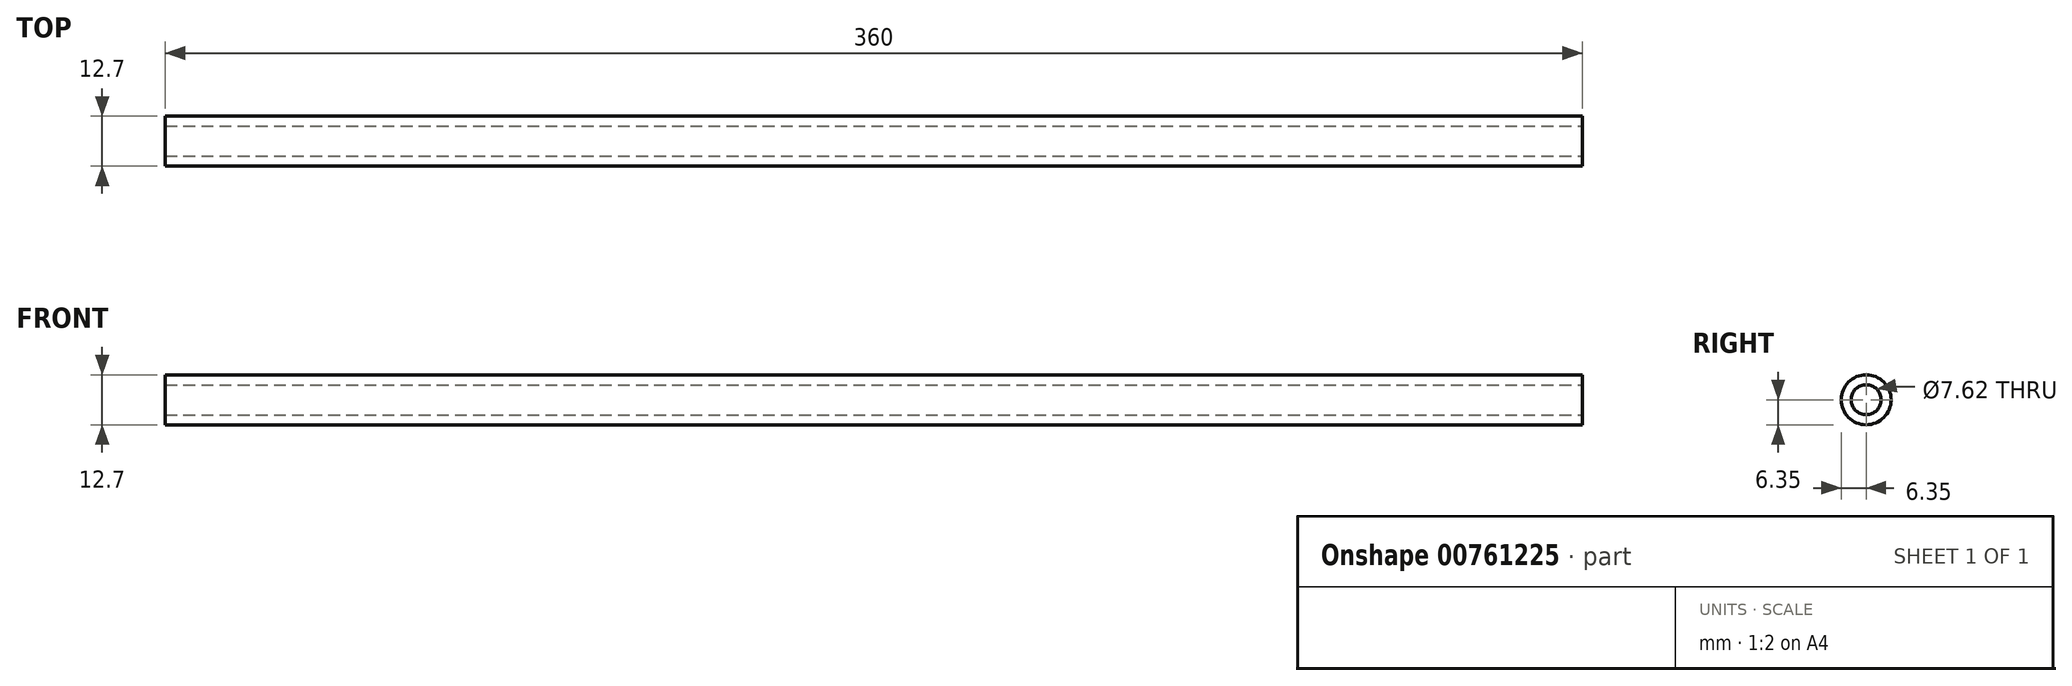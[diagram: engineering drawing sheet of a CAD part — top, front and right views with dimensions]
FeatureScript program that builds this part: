
annotation { "Feature Type Name" : "Feature", "Feature Type Description" : "" }
export const myFeature = defineFeature(function(context is Context, id is Id, definition is map)
    precondition{}
    {
        {
            var Q0;
            Q0=qCreatedBy(makeId("Front.planeOp"),FACE);
            var sketch = newSketch(context, id + "F0", { "sketchPlane" : qUnion([Q0])});
            skLineSegment(sketch, "E0", {"start": v(0, 3.8) * mm, "end": v(-360, 3.8) * mm});
            skLineSegment(sketch, "E1", {"start": v(-360, 3.8) * mm, "end": v(-360, 6.35) * mm});
            skLineSegment(sketch, "E2", {"start": v(-360, 6.35) * mm, "end": v(0, 6.35) * mm});
            skLineSegment(sketch, "E3", {"start": v(0, 6.35) * mm, "end": v(0, 3.8) * mm});
            skLineSegment(sketch, "E4", {"start": v(0, 0) * mm, "end": v(-360, 0) * mm, "construction": true});
            skSolve(sketch);
        }
        {
            var Q0;
            Q0=makeQuery(id+"F0.imprint","IMPRINT",FACE,{"disambiguationData":[TD([[makeQuery(id+"F0.imprint","IMPRINT",EDGE,{"derivedFrom":sQuery(id+"F0.wireOp",EDGE,"E0")}),-1.0]])]});
            var Q1;
            Q1=sQuery(id+"F0.wireOp",EDGE,"E1");
            var Q2;
            Q2=sQuery(id+"F0.wireOp",EDGE,"E2");
            var Q3;
            Q3=sQuery(id+"F0.wireOp",EDGE,"E3");
            var Q4;
            Q4=sQuery(id+"F0.wireOp",EDGE,"E0");
            var Q5;
            Q5=sQuery(id+"F0.wireOp",EDGE,"E4");
            revolve(context, id + "F1", {"surfaceOperationType" : NewSurfaceOperationType.NEW, "entities" : qUnion([Q0]), "surfaceEntities" : qUnion([Q1, Q2, Q3, Q4]), "axis" : qUnion([Q5]), "revolveType" : RevolveType.FULL});
        }
    });
